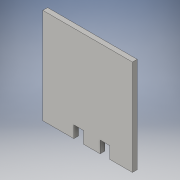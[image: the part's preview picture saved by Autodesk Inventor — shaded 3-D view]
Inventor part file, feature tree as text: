
AUTODESK INVENTOR PART (.ipt)
format: ipt  version: 2016 (Build 200138000, 138)  size: 107,008 bytes
history: native  units: in
note: dims shown in document units (in); Inventor stores cm internally (conversion verified against a paired STEP export)
features: sketch x2, extrude x1
ambient origin geometry x8: Origin, YZ Plane, XZ Plane, XY Plane, X Axis, Y Axis, Z Axis, Center Point
bodies: Solid1 (feature_tree)
feature tree (3):
  sketch  "Sketch1"  dims[d1=10.0in d2=5.125in]
  extrude  "Extrusion1"  Depth=5.125in
  sketch  "Sketch2"  dims[d3=0.875in d4=1.0in d5=0.875in d6=1.0in d7=1.25in d8=0.5in d9=0.0in]
